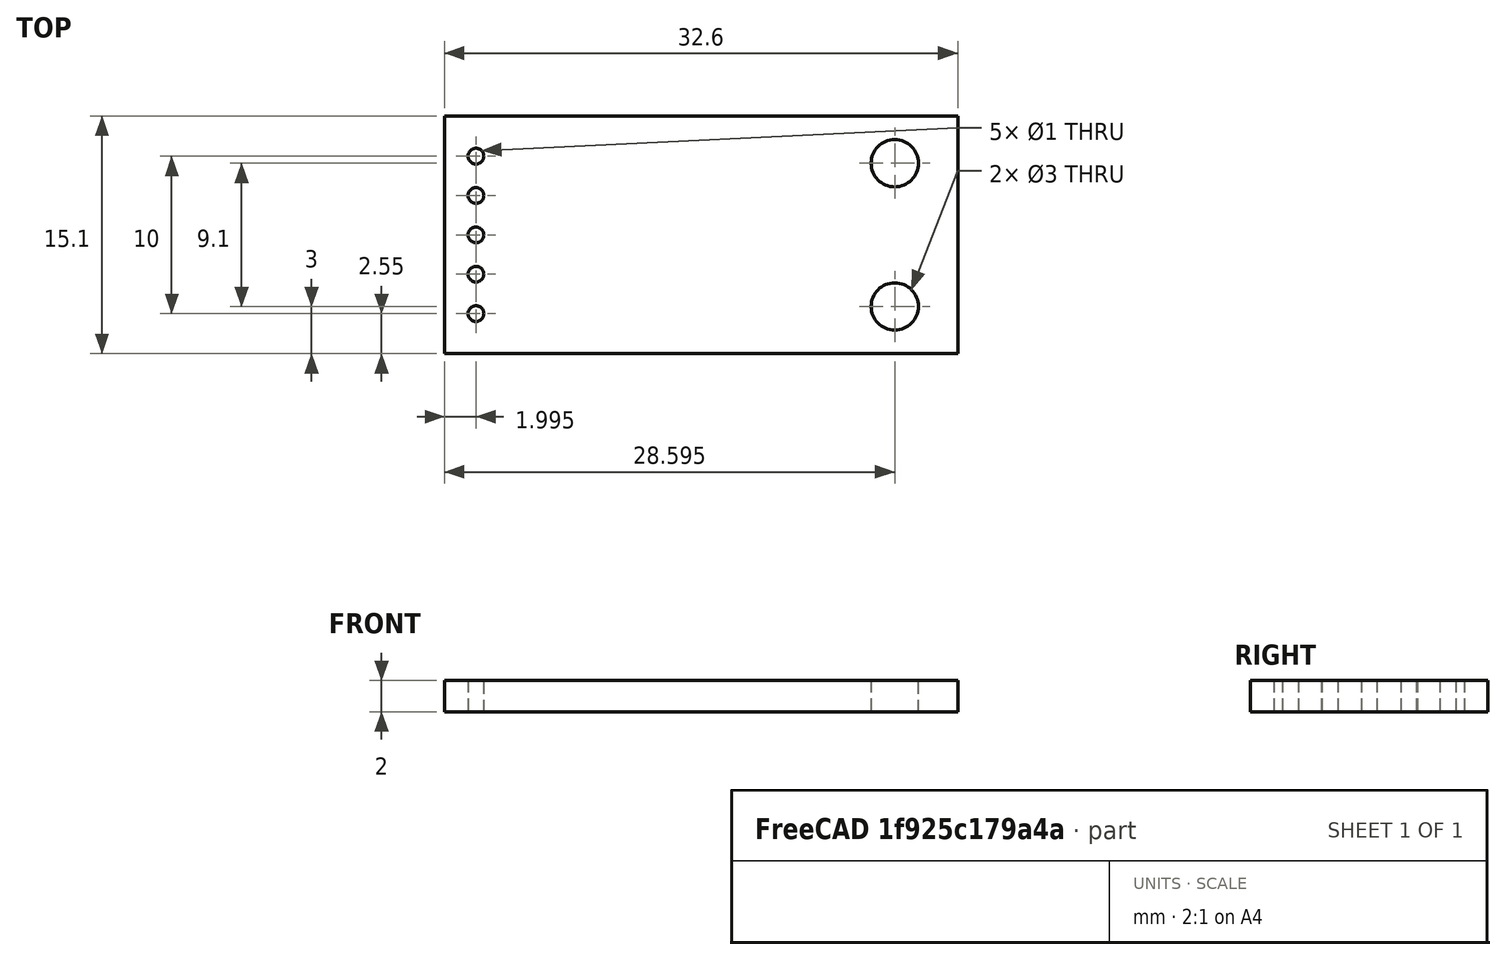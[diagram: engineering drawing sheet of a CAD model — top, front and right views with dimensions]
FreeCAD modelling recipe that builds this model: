
FCSTD DOCUMENT  (FreeCAD 0.16R6712 (Git))
Label: BH1750FVI
License: All rights reserved
LicenseURL: http://en.wikipedia.org/wiki/All_rights_reserved
objects: Sketcher::SketchObject×1, PartDesign::Pad×1
note: 3 computed .brp shape members not serialized (recipe doc carries the construction recipe); baked Part::Feature solids carry a one-line shape summary decoded from their .brp

FEATURE [Sketcher::SketchObject] Sketch
  sketch-geometry (11):
    g0: LineSegment StartX=0.0152782 StartY=15.1 StartZ=0 EndX=32.6153 EndY=15.1 EndZ=0
    g1: LineSegment StartX=32.6153 StartY=15.1 StartZ=0 EndX=32.6153 EndY=0 EndZ=0
    g2: LineSegment StartX=32.6153 StartY=0 StartZ=0 EndX=0.0152782 EndY=0 EndZ=0
    g3: LineSegment StartX=0.0152782 StartY=0 StartZ=0 EndX=0.0152782 EndY=15.1 EndZ=0
    g4: Circle CenterX=2.01528 CenterY=12.55 CenterZ=0 NormalX=0 NormalY=0 NormalZ=1 Radius=0.5
    g5: Circle CenterX=2.01528 CenterY=10.05 CenterZ=0 NormalX=0 NormalY=0 NormalZ=1 Radius=0.5
    g6: Circle CenterX=2.01528 CenterY=7.55 CenterZ=0 NormalX=0 NormalY=0 NormalZ=1 Radius=0.5
    g7: Circle CenterX=2.01528 CenterY=5.05 CenterZ=0 NormalX=0 NormalY=0 NormalZ=1 Radius=0.5
    g8: Circle CenterX=2.01528 CenterY=2.55 CenterZ=0 NormalX=0 NormalY=0 NormalZ=1 Radius=0.5
    g9: Circle CenterX=28.6153 CenterY=12.1 CenterZ=0 NormalX=0 NormalY=0 NormalZ=1 Radius=1.5
    g10: Circle CenterX=28.6153 CenterY=3 CenterZ=0 NormalX=0 NormalY=0 NormalZ=1 Radius=1.5
  constraints (33):
    c: Coincident(g0,g1)
    c: Coincident(g1,g2)
    c: Coincident(g2,g3)
    c: Coincident(g3,g0)
    c: Horizontal(g2)
    c: Vertical(g1)
    c: Vertical(g3)
    c: PointOnObject(g1,g-1)
    c: Equal(g3,g1)
    c: Equal(g0,g2)
    c: Distance(g3) = 15.1
    c: Distance(g0) = 32.6
    c: Distance(g4,g3) = 2
    c: Radius(g4) = 0.5
    c: Distance(g5,g4) = 2.5
    c: Distance(g5,g3) = 2
    c: Distance(g6,g3) = 2
    c: Distance(g7,g3) = 2
    c: Distance(g5,g6) = 2.5
    c: Radius(g5) = 0.5
    c: Radius(g6) = 0.5
    c: Radius(g7) = 0.5
    c: Radius(g8) = 0.5
    c: Distance(g6,g7) = 2.5
    c: Distance(g8,g7) = 2.5
    c: Radius(g9) = 1.5
    c: Radius(g10) = 1.5
    c: Distance(g9,g0) = 3
    c: Distance(g9,g1) = 4
    c: Distance(g10,g1) = 4
    c: DistanceY(g-1,g10) = 3
    c: Distance(g6,g2) = 7.55
    c: Distance(g8,g3) = 2
FEATURE [PartDesign::Pad] Pad  label="BH1750FVI -- measured no datasheer"
  Length = 2
  Length2 = 100
  Sketch = -> Sketch
  Type = 0
